# Revit family: Bath-Freestanding-KOHLER-Landshapes-K-32131_1
name_source: partatom
category: Plumbing Fixtures
units: mm (PartAtom-declared; Revit-internal decimal feet)

## family parameters
Cut with Voids When Loaded = No
Host = Face
OmniClass Number = 23.31.15.00
OmniClass Title = Bathtubs
Part Type = Normal
Room Calculation Point = No
Round Connector Dimension = Use Diameter
Shared = No

## types (1)
- HW1-Honed White
    ADA Compliant = No
    Assembly Code = D2010500
    CW Connection = No
    Cold Water Inlet = Cold Water Inlet
    Date Modified = 01/10/2024
    Default Elevation = 0"
    Description = DANIEL ARSHAM BATH
    Drain Included = No
    Finish = Kohler-Lithocast-HW1-Honed_White
    HW Connection = No
    Height = 24"
    Hot Water Inlet = Hot Water Inlet
    Length = 69 9/16"
    Manufacturer = Kohler Co.
    Master Format 2014 = 22 41 19
    Master Format 2014 Name = Residential Bathtubs
    Material = Lithocast
    Model = K-32131-HW1
    Product Documentation Link = https://www.us.kohler.com
    Product Name = Landshapes
    Product Page URL = http://www.us.kohler.com
    Type = 1
    URL = https://www.us.kohler.com
    Vent Connection = No
    Waste Connection = Yes
    Waste Water Outlet = Waste Water Outlet
    WaterSense Certified = No
    Width = 34 7/16"

## geometry (parser evidence)
native form markers: Sweep x6
no freeform markers — native parametric forms only
